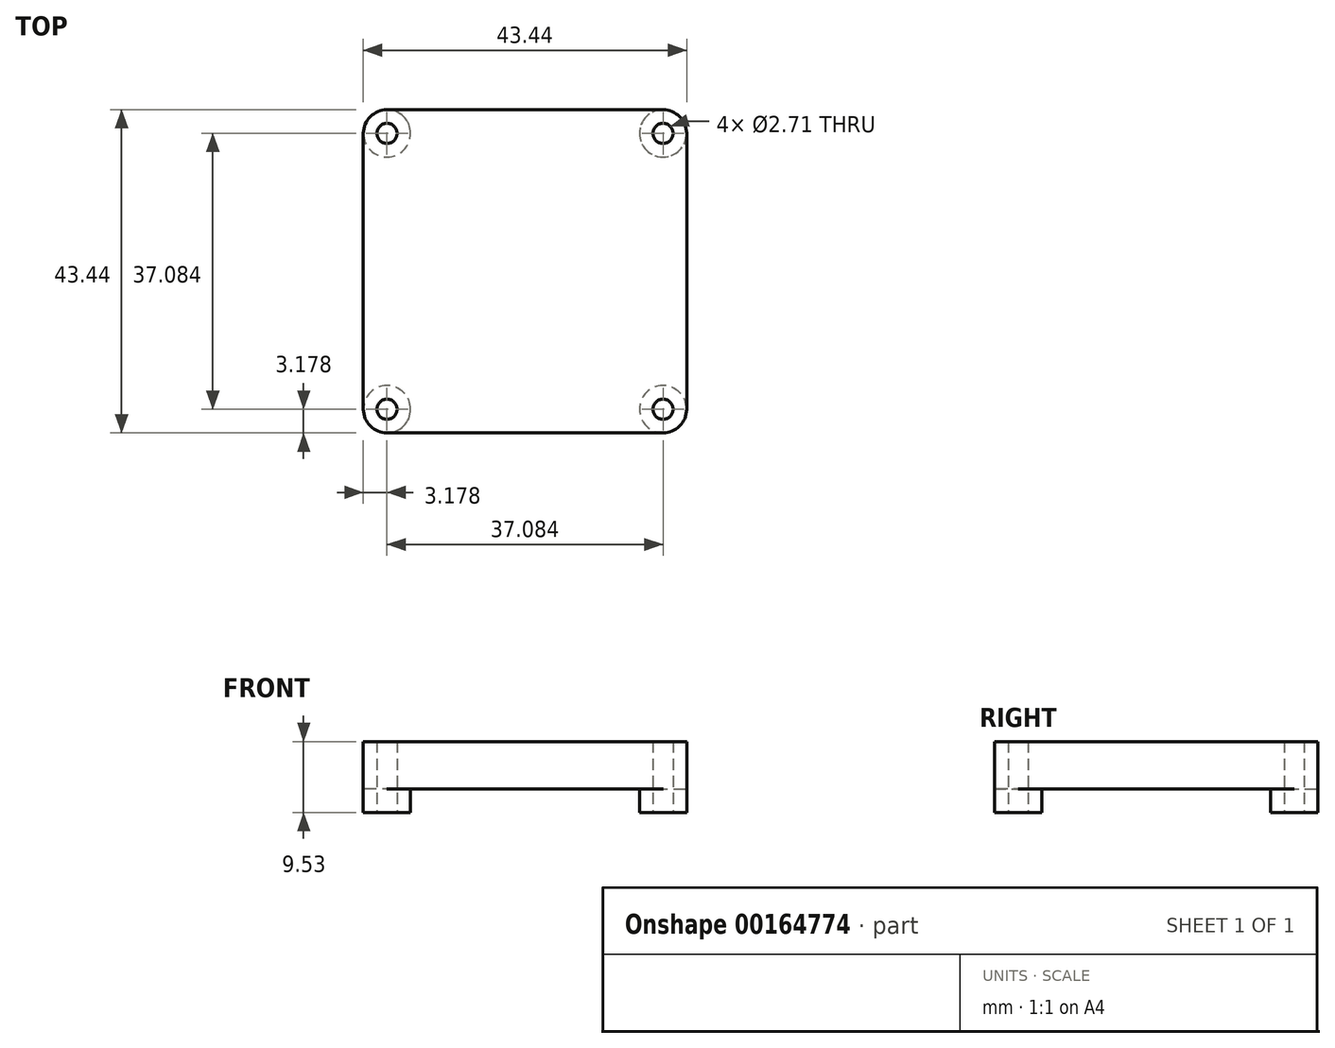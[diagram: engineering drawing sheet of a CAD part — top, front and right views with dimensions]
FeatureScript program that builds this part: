
annotation { "Feature Type Name" : "Feature", "Feature Type Description" : "" }
export const myFeature = defineFeature(function(context is Context, id is Id, definition is map)
    precondition{}
    {
        {
            var Q0;
            Q0=qCreatedBy(makeId("Top.planeOp"),FACE);
            var sketch = newSketch(context, id + "F0", { "sketchPlane" : qUnion([Q0])});
            skLineSegment(sketch, "E0.bottom", {"start": v(21.72, 21.72) * mm, "end": v(-21.72, 21.72) * mm});
            skLineSegment(sketch, "E0.top", {"start": v(21.72, -21.72) * mm, "end": v(-21.72, -21.72) * mm});
            skLineSegment(sketch, "E0.left", {"start": v(21.72, 21.72) * mm, "end": v(21.72, -21.72) * mm});
            skLineSegment(sketch, "E0.right", {"start": v(-21.72, 21.72) * mm, "end": v(-21.72, -21.72) * mm});
            skPoint(sketch, "E0.middle", {"position": v(0, 0) * mm});
            skLineSegment(sketch, "E1.bottom", {"start": v(18.54, 18.54) * mm, "end": v(-18.54, 18.54) * mm, "construction": true});
            skLineSegment(sketch, "E1.top", {"start": v(18.54, -18.54) * mm, "end": v(-18.54, -18.54) * mm, "construction": true});
            skLineSegment(sketch, "E1.left", {"start": v(18.54, 18.54) * mm, "end": v(18.54, -18.54) * mm, "construction": true});
            skLineSegment(sketch, "E1.right", {"start": v(-18.54, 18.54) * mm, "end": v(-18.54, -18.54) * mm, "construction": true});
            skCircle(sketch, "E2", {"center": v(-18.54, 18.54) * mm, "radius": 1.35 * mm});
            skCircle(sketch, "E3", {"center": v(18.54, 18.54) * mm, "radius": 1.35 * mm});
            skCircle(sketch, "E4", {"center": v(18.54, -18.54) * mm, "radius": 1.35 * mm});
            skCircle(sketch, "E5", {"center": v(-18.54, -18.54) * mm, "radius": 1.35 * mm});
            skSolve(sketch);
        }
        {
            var Q0;
            Q0 = qSketchRegion(id + "F0", true);
            extrude(context, id + "F1", {"entities" : qUnion([Q0]), "depth" : 6.35 * mm});
        }
        {
            var Q0;
            Q0=makeQuery(id+"F1.opExtrude","SWEPT_EDGE",EDGE,{"disambiguationData":[OSD([sQuery(id+"F0.wireOp",EDGE,"E0.bottom"),sQuery(id+"F0.wireOp",EDGE,"E0.right")])]});
            var Q1;
            Q1=makeQuery(id+"F1.opExtrude","SWEPT_EDGE",EDGE,{"disambiguationData":[OSD([sQuery(id+"F0.wireOp",EDGE,"E0.bottom"),sQuery(id+"F0.wireOp",EDGE,"E0.left")])]});
            var Q2;
            Q2=makeQuery(id+"F1.opExtrude","SWEPT_EDGE",EDGE,{"disambiguationData":[OSD([sQuery(id+"F0.wireOp",EDGE,"E0.top"),sQuery(id+"F0.wireOp",EDGE,"E0.left")])]});
            var Q3;
            Q3=makeQuery(id+"F1.opExtrude","SWEPT_EDGE",EDGE,{"disambiguationData":[OSD([sQuery(id+"F0.wireOp",EDGE,"E0.top"),sQuery(id+"F0.wireOp",EDGE,"E0.right")])]});
            fillet(context, id + "F2", {"entities" : qUnion([Q0, Q1, Q2, Q3]), "radius" : 3.17 * mm, "allowEdgeOverflow" : false});
        }
        {
            var Q0;
            Q0=makeQuery(id+"F1.opExtrude","CAP_FACE",FACE,{"disambiguationData":[OSD([sQuery(id+"F0.wireOp",EDGE,"E0.bottom"),sQuery(id+"F0.wireOp",EDGE,"E0.top"),sQuery(id+"F0.wireOp",EDGE,"E0.left"),sQuery(id+"F0.wireOp",EDGE,"E0.right"),sQuery(id+"F0.wireOp",EDGE,"E2"),sQuery(id+"F0.wireOp",EDGE,"E3"),sQuery(id+"F0.wireOp",EDGE,"E4"),sQuery(id+"F0.wireOp",EDGE,"E5")])],"isStart":true});
            var sketch = newSketch(context, id + "F3", { "sketchPlane" : qUnion([Q0])});
            skCircle(sketch, "E6", {"center": v(18.54, 18.54) * mm, "radius": 1.35 * mm});
            skCircle(sketch, "E7", {"center": v(18.54, 18.54) * mm, "radius": 3.18 * mm});
            skCircle(sketch, "E8", {"center": v(18.54, -18.54) * mm, "radius": 1.35 * mm});
            skCircle(sketch, "E9", {"center": v(18.54, -18.54) * mm, "radius": 3.18 * mm});
            skCircle(sketch, "E10", {"center": v(-18.54, -18.54) * mm, "radius": 1.35 * mm});
            skCircle(sketch, "E11", {"center": v(-18.54, -18.54) * mm, "radius": 3.18 * mm});
            skCircle(sketch, "E12", {"center": v(-18.54, 18.54) * mm, "radius": 1.35 * mm});
            skCircle(sketch, "E13", {"center": v(-18.54, 18.54) * mm, "radius": 3.18 * mm});
            skSolve(sketch);
        }
        {
            var Q0;
            Q0 = qSketchRegion(id + "F3", true);
            extrude(context, id + "F4", {"entities" : qUnion([Q0]), "operationType" : NewBodyOperationType.ADD, "depth" : 3.17 * mm});
        }
    });
